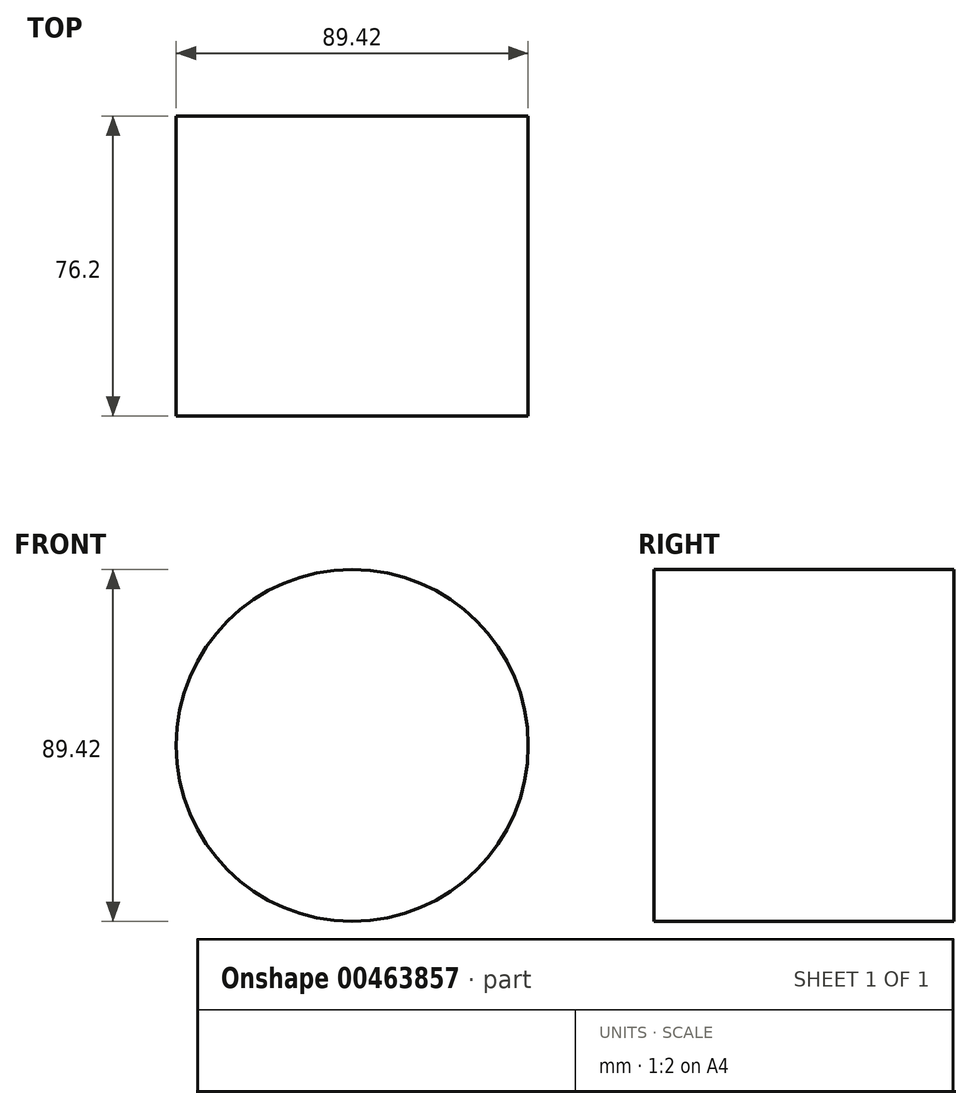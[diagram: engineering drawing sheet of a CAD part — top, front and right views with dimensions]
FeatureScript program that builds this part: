
annotation { "Feature Type Name" : "Feature", "Feature Type Description" : "" }
export const myFeature = defineFeature(function(context is Context, id is Id, definition is map)
    precondition{}
    {
        {
            var Q0;
            Q0=qCreatedBy(makeId("Front.planeOp"),FACE);
            var sketch = newSketch(context, id + "F0", { "sketchPlane" : qUnion([Q0])});
            skCircle(sketch, "E0", {"center": v(0, 0) * mm, "radius": 44.71 * mm});
            skSolve(sketch);
        }
        {
            var Q0;
            Q0=makeQuery(id+"F0.imprint","IMPRINT",FACE,{"disambiguationData":[TD([[makeQuery(id+"F0.imprint","IMPRINT",EDGE,{"derivedFrom":sQuery(id+"F0.wireOp",EDGE,"E0")}),1.0]])]});
            extrude(context, id + "F1", {"entities" : qUnion([Q0]), "depth" : 76.2 * mm});
        }
    });
